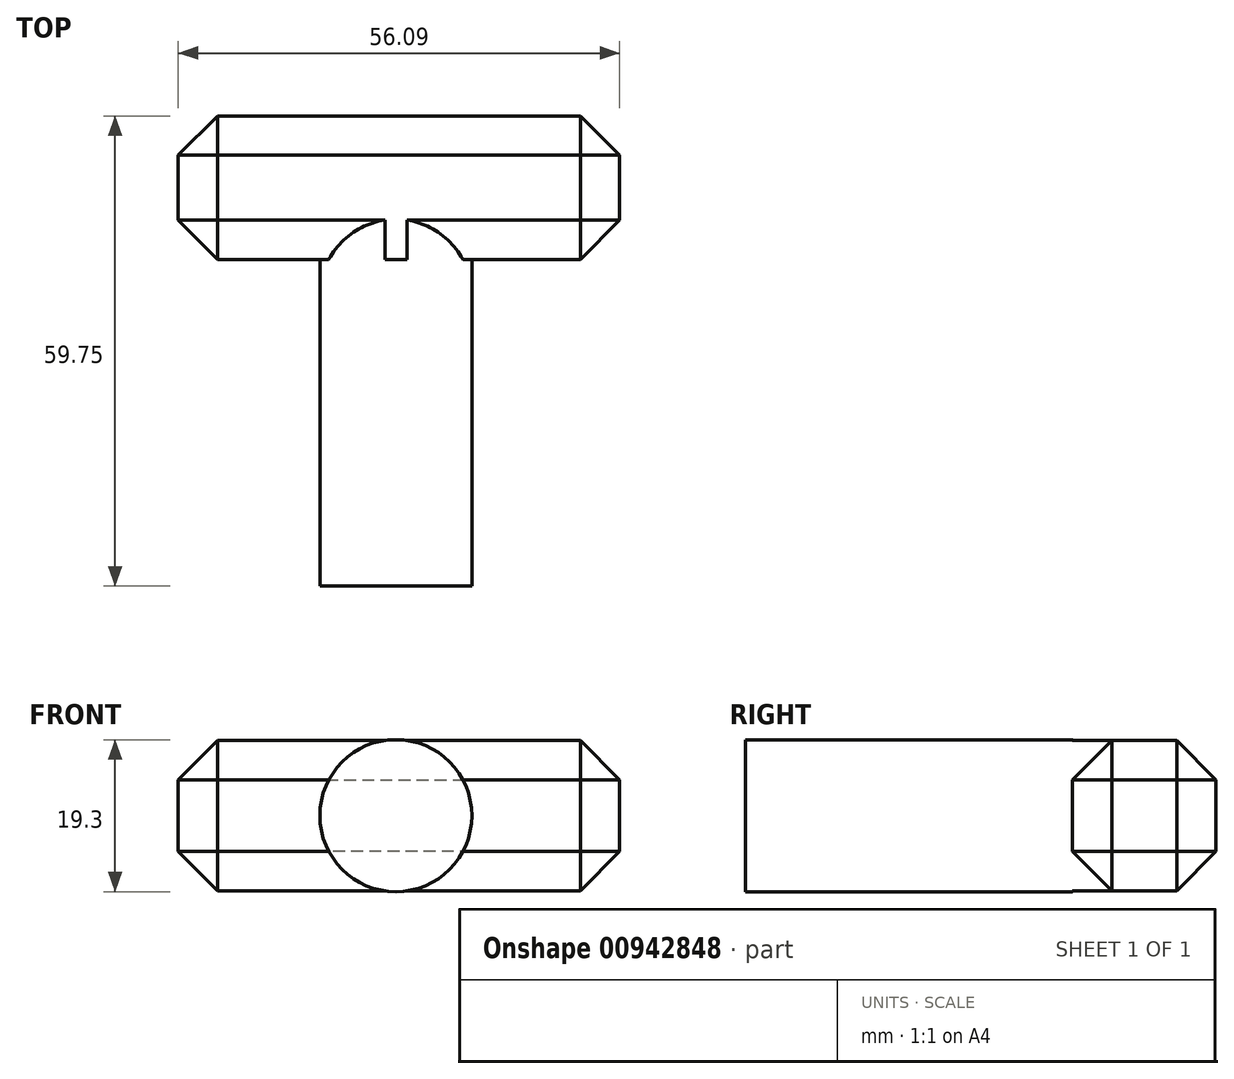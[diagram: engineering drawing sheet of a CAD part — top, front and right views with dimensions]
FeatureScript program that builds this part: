
annotation { "Feature Type Name" : "Feature", "Feature Type Description" : "" }
export const myFeature = defineFeature(function(context is Context, id is Id, definition is map)
    precondition{}
    {
        {
            var Q0;
            Q0=qCreatedBy(makeId("Top.planeOp"),FACE);
            var sketch = newSketch(context, id + "F0", { "sketchPlane" : qUnion([Q0])});
            skLineSegment(sketch, "E0.left", {"start": v(-9.65, -3.2) * mm, "end": v(-9.65, 29.2) * mm});
            skLineSegment(sketch, "E1.bottom", {"start": v(-27.65, 47.44) * mm, "end": v(28.44, 47.44) * mm});
            skLineSegment(sketch, "E1.top", {"start": v(-27.65, 29.2) * mm, "end": v(-9.65, 29.2) * mm});
            skLineSegment(sketch, "E1.left", {"start": v(-27.65, 47.44) * mm, "end": v(-27.65, 29.2) * mm});
            skLineSegment(sketch, "E1.right", {"start": v(28.44, 47.44) * mm, "end": v(28.44, 29.2) * mm});
            skLineSegment(sketch, "E2.trimOffspring", {"start": v(10.44, 29.2) * mm, "end": v(28.44, 29.2) * mm});
            skLineSegment(sketch, "E3", {"start": v(-9.65, -3.2) * mm, "end": v(-9.65, -12.3) * mm});
            skLineSegment(sketch, "E4", {"start": v(-9.65, -12.3) * mm, "end": v(0, -12.3) * mm});
            skLineSegment(sketch, "E5", {"start": v(10.44, 29.2) * mm, "end": v(-9.65, 29.2) * mm});
            skLineSegment(sketch, "E6", {"start": v(0, 29.2) * mm, "end": v(0, -12.3) * mm});
            skPoint(sketch, "E6.endSnap0", {"position": v(0.4, -12.3) * mm});
            skPoint(sketch, "E7.orphan", {"position": v(10.44, -12.3) * mm});
            skSolve(sketch);
        }
        {
            var Q0;
            {var subQ1=sQuery(id+"F0.wireOp",EDGE,"E0.left");Q0=makeQuery(id+"F0.imprint","IMPRINT",FACE,{"disambiguationData":[TD([[makeQuery(id+"F0.imprint","IMPRINT",EDGE,{"derivedFrom":subQ1}),-1.0]])]});}
            var Q1;
            Q1=sQuery(id+"F0.wireOp",EDGE,"E6");
            revolve(context, id + "F1", {"surfaceOperationType" : NewSurfaceOperationType.NEW, "entities" : qUnion([Q0]), "axis" : qUnion([Q1]), "revolveType" : RevolveType.FULL});
        }
        {
            var Q0;
            Q0=makeQuery(id+"F0.imprint","IMPRINT",FACE,{"disambiguationData":[TD([[makeQuery(id+"F0.imprint","IMPRINT",EDGE,{"derivedFrom":sQuery(id+"F0.wireOp",EDGE,"E1.bottom")}),-1.0]])]});
            extrude(context, id + "F2", {"entities" : qUnion([Q0]), "operationType" : NewBodyOperationType.ADD, "endBound" : BoundingType.SYMMETRIC, "depth" : 19.1 * mm, "offsetDistance" : 25 * mm});
        }
        {
            var Q0;
            Q0=makeQuery(id+"F2.opExtrude","SWEPT_EDGE",EDGE,{"disambiguationData":[OSD([sQuery(id+"F0.wireOp",EDGE,"E1.bottom"),sQuery(id+"F0.wireOp",EDGE,"E1.right")])]});
            var Q1;
            Q1=makeQuery(id+"F2.opExtrude","CAP_EDGE",EDGE,{"disambiguationData":[OSD([sQuery(id+"F0.wireOp",EDGE,"E1.bottom")])],"isStart":false});
            var Q2;
            Q2=makeQuery(id+"F2.opExtrude","CAP_EDGE",EDGE,{"disambiguationData":[OSD([sQuery(id+"F0.wireOp",EDGE,"E1.right")])],"isStart":false});
            var Q3;
            Q3=makeQuery(id+"F2.opExtrude","SWEPT_EDGE",EDGE,{"disambiguationData":[OSD([sQuery(id+"F0.wireOp",EDGE,"E1.right"),sQuery(id+"F0.wireOp",EDGE,"E2.trimOffspring")])]});
            var Q4;
            Q4=makeQuery(id+"F2.opExtrude","CAP_EDGE",EDGE,{"disambiguationData":[OSD([sQuery(id+"F0.wireOp",EDGE,"E1.right")])],"isStart":true});
            var Q5;
            {var subQ0=sQuery(id+"F0.wireOp",EDGE,"E5");var subQ1=sQuery(id+"F0.wireOp",EDGE,"E2.trimOffspring");var subQ2=sQuery(id+"F0.wireOp",EDGE,"E1.top");var subQ3=makeQuery(id+"F2.opExtrude","SWEPT_FACE",FACE,{"disambiguationData":[OSD([subQ2,subQ1,subQ0])]});var subQ4=sQuery(id+"F0.wireOp",EDGE,"E1.right");var subQ5=makeQuery(id+"F2.opExtrude","CAP_FACE",FACE,{"disambiguationData":[OSD([sQuery(id+"F0.wireOp",EDGE,"E1.bottom"),subQ2,sQuery(id+"F0.wireOp",EDGE,"E1.left"),subQ4,subQ1,subQ0])],"isStart":false});Q5=makeQuery(id+"F2.boolean.opBoolean","SPLIT",EDGE,{"disambiguationData":[topologyDisambiguationEdgeConnected([subQ5,subQ3]),TD([makeQuery(id+"F2.opExtrude","SWEPT_FACE",FACE,{"disambiguationData":[OSD([subQ4])]})])],"derivedFrom":makeQuery(id+"F2.opExtrude","CAP_EDGE",EDGE,{"disambiguationData":[OSD([subQ2,subQ1,subQ0])],"isStart":false})});}
            var Q6;
            Q6=makeQuery(id+"F2.opExtrude","CAP_FACE",FACE,{"disambiguationData":[OSD([sQuery(id+"F0.wireOp",EDGE,"E1.bottom"),sQuery(id+"F0.wireOp",EDGE,"E1.top"),sQuery(id+"F0.wireOp",EDGE,"E1.left"),sQuery(id+"F0.wireOp",EDGE,"E1.right"),sQuery(id+"F0.wireOp",EDGE,"E2.trimOffspring"),sQuery(id+"F0.wireOp",EDGE,"E5")])],"isStart":false});
            var Q7;
            {var subQ0=sQuery(id+"F0.wireOp",EDGE,"E5");var subQ1=sQuery(id+"F0.wireOp",EDGE,"E2.trimOffspring");var subQ2=sQuery(id+"F0.wireOp",EDGE,"E1.top");var subQ3=makeQuery(id+"F2.opExtrude","SWEPT_FACE",FACE,{"disambiguationData":[OSD([subQ2,subQ1,subQ0])]});var subQ4=sQuery(id+"F0.wireOp",EDGE,"E1.right");var subQ5=makeQuery(id+"F2.opExtrude","CAP_FACE",FACE,{"disambiguationData":[OSD([sQuery(id+"F0.wireOp",EDGE,"E1.bottom"),subQ2,sQuery(id+"F0.wireOp",EDGE,"E1.left"),subQ4,subQ1,subQ0])],"isStart":true});Q7=makeQuery(id+"F2.boolean.opBoolean","SPLIT",EDGE,{"disambiguationData":[topologyDisambiguationEdgeConnected([subQ5,subQ3]),TD([makeQuery(id+"F2.opExtrude","SWEPT_FACE",FACE,{"disambiguationData":[OSD([subQ4])]})])],"derivedFrom":makeQuery(id+"F2.opExtrude","CAP_EDGE",EDGE,{"disambiguationData":[OSD([subQ2,subQ1,subQ0])],"isStart":true})});}
            var Q8;
            {var subQ0=sQuery(id+"F0.wireOp",EDGE,"E5");var subQ1=sQuery(id+"F0.wireOp",EDGE,"E2.trimOffspring");var subQ2=sQuery(id+"F0.wireOp",EDGE,"E1.top");var subQ3=makeQuery(id+"F2.opExtrude","SWEPT_FACE",FACE,{"disambiguationData":[OSD([subQ2,subQ1,subQ0])]});var subQ4=sQuery(id+"F0.wireOp",EDGE,"E1.left");var subQ5=makeQuery(id+"F2.opExtrude","CAP_FACE",FACE,{"disambiguationData":[OSD([sQuery(id+"F0.wireOp",EDGE,"E1.bottom"),subQ2,subQ4,sQuery(id+"F0.wireOp",EDGE,"E1.right"),subQ1,subQ0])],"isStart":true});Q8=makeQuery(id+"F2.boolean.opBoolean","SPLIT",EDGE,{"disambiguationData":[topologyDisambiguationEdgeConnected([subQ5,subQ3]),TD([makeQuery(id+"F2.opExtrude","SWEPT_FACE",FACE,{"disambiguationData":[OSD([subQ4])]})])],"derivedFrom":makeQuery(id+"F2.opExtrude","CAP_EDGE",EDGE,{"disambiguationData":[OSD([subQ2,subQ1,subQ0])],"isStart":true})});}
            var Q9;
            Q9=makeQuery(id+"F2.opExtrude","SWEPT_EDGE",EDGE,{"disambiguationData":[OSD([sQuery(id+"F0.wireOp",EDGE,"E1.top"),sQuery(id+"F0.wireOp",EDGE,"E1.left")])]});
            var Q10;
            Q10=makeQuery(id+"F2.opExtrude","CAP_EDGE",EDGE,{"disambiguationData":[OSD([sQuery(id+"F0.wireOp",EDGE,"E1.left")])],"isStart":true});
            var Q11;
            Q11=makeQuery(id+"F2.opExtrude","SWEPT_EDGE",EDGE,{"disambiguationData":[OSD([sQuery(id+"F0.wireOp",EDGE,"E1.bottom"),sQuery(id+"F0.wireOp",EDGE,"E1.left")])]});
            var Q12;
            Q12=makeQuery(id+"F2.opExtrude","CAP_EDGE",EDGE,{"disambiguationData":[OSD([sQuery(id+"F0.wireOp",EDGE,"E1.bottom")])],"isStart":true});
            chamfer(context, id + "F3", {"entities" : qUnion([Q0, Q1, Q2, Q3, Q4, Q5, Q6, Q7, Q8, Q9, Q10, Q11, Q12]), "width" : 5 * mm, "tangentPropagation" : true});
        }
    });
